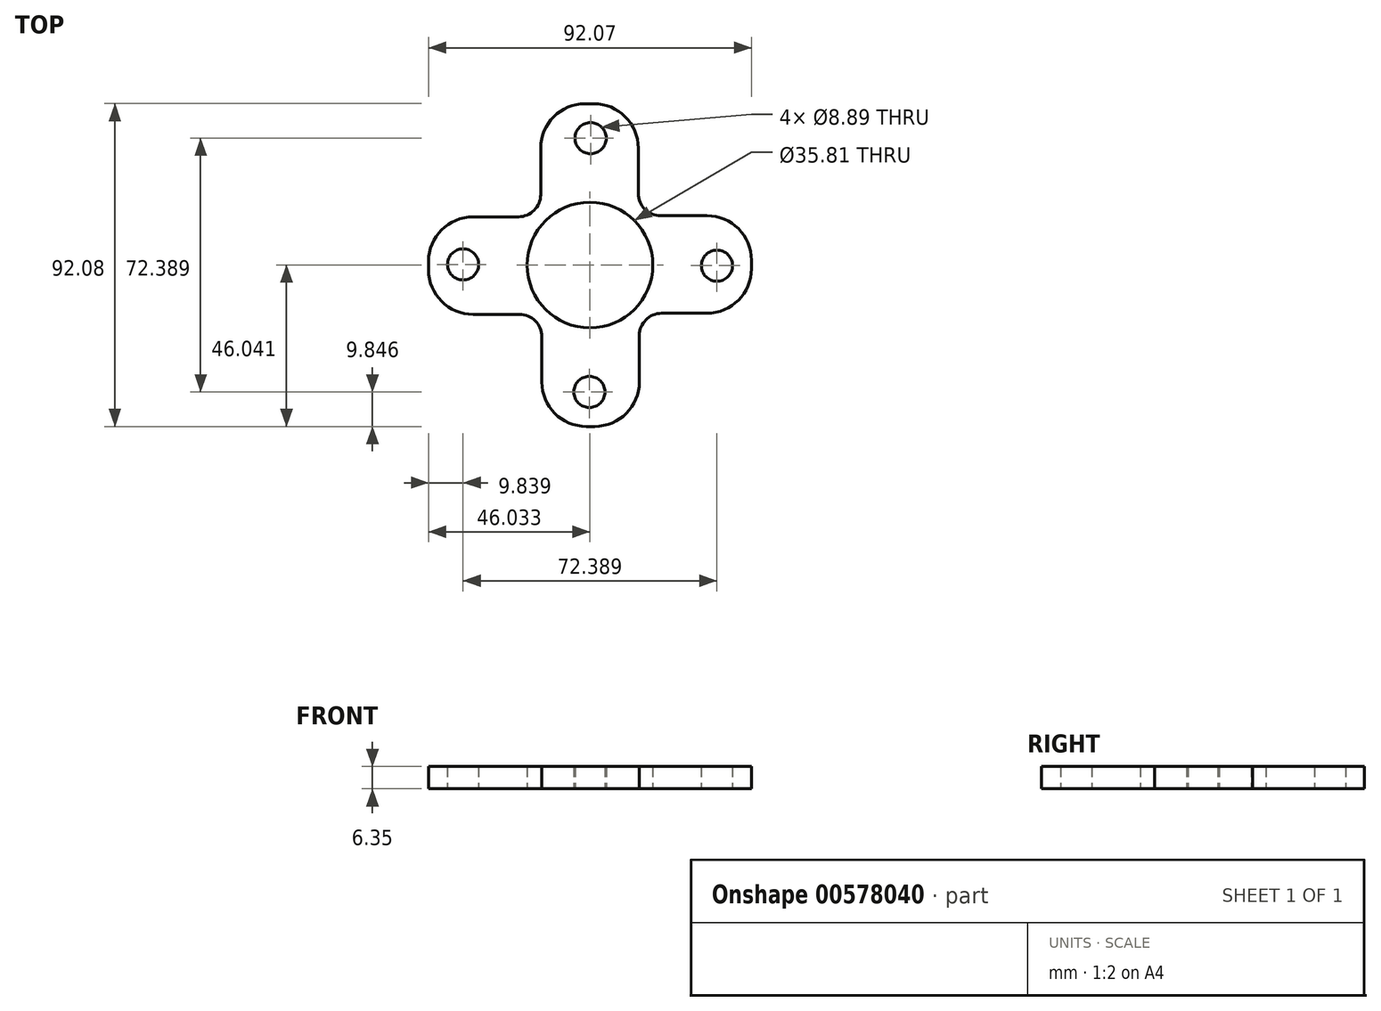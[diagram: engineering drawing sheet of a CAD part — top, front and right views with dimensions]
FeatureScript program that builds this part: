
annotation { "Feature Type Name" : "Feature", "Feature Type Description" : "" }
export const myFeature = defineFeature(function(context is Context, id is Id, definition is map)
    precondition{}
    {
        {
            var Q0;
            Q0=qCreatedBy(makeId("Top.planeOp"),FACE);
            var sketch = newSketch(context, id + "F0", { "sketchPlane" : qUnion([Q0])});
            skCircle(sketch, "E0", {"center": v(7.05, -2.28) * mm, "radius": 36.2 * mm, "construction": true});
            skCircle(sketch, "E1", {"center": v(7.05, -2.28) * mm, "radius": 17.9 * mm});
            skCircle(sketch, "E2", {"center": v(7.05, -2.28) * mm, "radius": 16.64 * mm});
            skCircle(sketch, "E3", {"center": v(43.25, -2.45) * mm, "radius": 4.45 * mm});
            skLineSegment(sketch, "E4.bottom", {"start": v(27.16, 11.8) * mm, "end": v(40.4, 11.8) * mm});
            skLineSegment(sketch, "E4.top", {"start": v(27.47, -16.04) * mm, "end": v(40.4, -16.04) * mm});
            skLineSegment(sketch, "E4.left", {"start": v(7.05, 11.8) * mm, "end": v(7.05, -16.04) * mm});
            skLineSegment(sketch, "E4.right", {"start": v(53.1, -0.9) * mm, "end": v(53.1, -3.34) * mm});
            skLineSegment(sketch, "E5.1.0", {"start": v(5.68, 43.76) * mm, "end": v(8.11, 43.76) * mm});
            skLineSegment(sketch, "E5.1.1", {"start": v(-7.02, 17.83) * mm, "end": v(-7.02, 31.06) * mm});
            skLineSegment(sketch, "E5.1.2", {"start": v(20.81, 18.14) * mm, "end": v(20.81, 31.06) * mm});
            skCircle(sketch, "E5.1.3", {"center": v(7.22, 33.92) * mm, "radius": 4.45 * mm});
            skLineSegment(sketch, "E5.2.0", {"start": v(-38.98, -3.65) * mm, "end": v(-38.98, -1.22) * mm});
            skLineSegment(sketch, "E5.2.1", {"start": v(-13.05, -16.35) * mm, "end": v(-26.28, -16.35) * mm});
            skLineSegment(sketch, "E5.2.2", {"start": v(-13.37, 11.48) * mm, "end": v(-26.28, 11.48) * mm});
            skCircle(sketch, "E5.2.3", {"center": v(-29.14, -2.1) * mm, "radius": 4.45 * mm});
            skLineSegment(sketch, "E5.3.0", {"start": v(8.42, -48.32) * mm, "end": v(6, -48.32) * mm});
            skLineSegment(sketch, "E5.3.1", {"start": v(21.12, -22.39) * mm, "end": v(21.12, -35.62) * mm});
            skLineSegment(sketch, "E5.3.2", {"start": v(-6.7, -22.7) * mm, "end": v(-6.7, -35.62) * mm});
            skCircle(sketch, "E5.3.3", {"center": v(6.88, -38.47) * mm, "radius": 4.45 * mm});
            skPoint(sketch, "E6.visualSharp", {"position": v(53.1, 11.8) * mm});
            skArc(sketch, "E6.filletArc", {"start": v(53.1, -0.9) * mm, "mid": v(49.37, 8.07) * mm, "end": v(40.4, 11.8) * mm});
            skPoint(sketch, "E7.visualSharp", {"position": v(53.1, -16.04) * mm});
            skArc(sketch, "E7.filletArc", {"start": v(40.4, -16.04) * mm, "mid": v(49.37, -12.32) * mm, "end": v(53.1, -3.34) * mm});
            skPoint(sketch, "E8.visualSharp", {"position": v(21.12, -48.32) * mm});
            skArc(sketch, "E8.filletArc", {"start": v(8.42, -48.32) * mm, "mid": v(17.4, -44.6) * mm, "end": v(21.12, -35.62) * mm});
            skPoint(sketch, "E9.visualSharp", {"position": v(-6.7, -48.32) * mm});
            skArc(sketch, "E9.filletArc", {"start": v(-6.7, -35.62) * mm, "mid": v(-2.99, -44.6) * mm, "end": v(6, -48.32) * mm});
            skPoint(sketch, "E10.visualSharp", {"position": v(-38.98, -16.35) * mm});
            skArc(sketch, "E10.filletArc", {"start": v(-38.98, -3.65) * mm, "mid": v(-35.26, -12.63) * mm, "end": v(-26.28, -16.35) * mm});
            skPoint(sketch, "E11.visualSharp", {"position": v(-38.98, 11.48) * mm});
            skArc(sketch, "E11.filletArc", {"start": v(-26.28, 11.48) * mm, "mid": v(-35.26, 7.76) * mm, "end": v(-38.98, -1.22) * mm});
            skPoint(sketch, "E12.visualSharp", {"position": v(-7.02, 43.76) * mm});
            skArc(sketch, "E12.filletArc", {"start": v(5.68, 43.76) * mm, "mid": v(-3.3, 40.04) * mm, "end": v(-7.02, 31.06) * mm});
            skPoint(sketch, "E13.visualSharp", {"position": v(20.81, 43.76) * mm});
            skArc(sketch, "E13.filletArc", {"start": v(20.81, 31.06) * mm, "mid": v(17.1, 40.04) * mm, "end": v(8.11, 43.76) * mm});
            skPoint(sketch, "E14.orphan", {"position": v(7.05, 11.48) * mm});
            skPoint(sketch, "E15.orphan", {"position": v(20.81, -2.28) * mm});
            skPoint(sketch, "E16.orphan", {"position": v(21.12, -2.28) * mm});
            skPoint(sketch, "E17.orphan", {"position": v(-6.7, -2.28) * mm});
            skPoint(sketch, "E18.orphan", {"position": v(-7.02, -2.28) * mm});
            skPoint(sketch, "E19.visualSharp", {"position": v(-7.02, 11.48) * mm});
            skArc(sketch, "E19.filletArc", {"start": v(-13.37, 11.48) * mm, "mid": v(-8.88, 13.34) * mm, "end": v(-7.02, 17.83) * mm});
            skPoint(sketch, "E20.visualSharp", {"position": v(20.81, 11.8) * mm});
            skArc(sketch, "E20.filletArc", {"start": v(20.81, 18.14) * mm, "mid": v(22.67, 13.65) * mm, "end": v(27.16, 11.8) * mm});
            skPoint(sketch, "E21.orphan", {"position": v(7.05, -16.35) * mm});
            skPoint(sketch, "E22.visualSharp", {"position": v(-6.7, -16.35) * mm});
            skArc(sketch, "E22.filletArc", {"start": v(-6.7, -22.7) * mm, "mid": v(-8.56, -18.2) * mm, "end": v(-13.05, -16.35) * mm});
            skPoint(sketch, "E23.visualSharp", {"position": v(21.12, -16.04) * mm});
            skArc(sketch, "E23.filletArc", {"start": v(27.47, -16.04) * mm, "mid": v(22.98, -17.9) * mm, "end": v(21.12, -22.39) * mm});
            skSolve(sketch);
        }
        {
            var Q0;
            Q0=makeQuery(id+"F0.imprint","IMPRINT",FACE,{"disambiguationData":[TD([[makeQuery(id+"F0.imprint","IMPRINT",EDGE,{"derivedFrom":sQuery(id+"F0.wireOp",EDGE,"E3")}),-1.0]])]});
            extrude(context, id + "F1", {"entities" : qUnion([Q0]), "depth" : 6.35 * mm, "offsetDistance" : 25.4 * mm});
        }
    });
